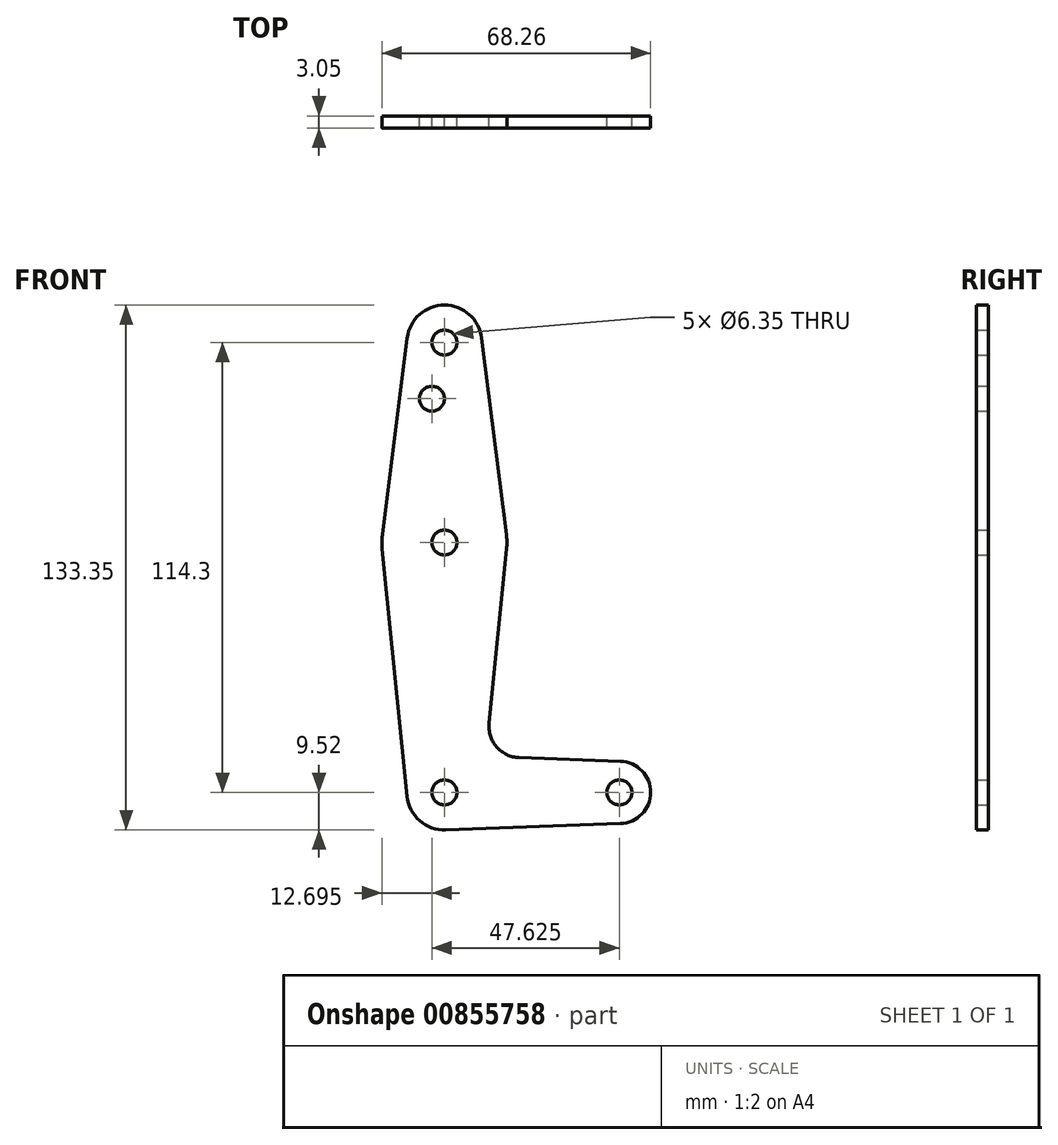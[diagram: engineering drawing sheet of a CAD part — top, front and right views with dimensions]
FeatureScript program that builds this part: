
annotation { "Feature Type Name" : "Feature", "Feature Type Description" : "" }
export const myFeature = defineFeature(function(context is Context, id is Id, definition is map)
    precondition{}
    {
        {
            var Q0;
            Q0=qCreatedBy(makeId("Front.planeOp"),FACE);
            var sketch = newSketch(context, id + "F0", { "sketchPlane" : qUnion([Q0])});
            skCircle(sketch, "E0", {"center": v(0, 0) * mm, "radius": 9.53 * mm});
            skLineSegment(sketch, "E1", {"start": v(0, 0) * mm, "end": v(0, 114.3) * mm, "construction": true});
            skCircle(sketch, "E2", {"center": v(0, 114.3) * mm, "radius": 9.53 * mm});
            skCircle(sketch, "E3", {"center": v(0, 63.5) * mm, "radius": 15.88 * mm});
            skLineSegment(sketch, "E4", {"start": v(0, 0) * mm, "end": v(44.45, 0) * mm, "construction": true});
            skCircle(sketch, "E5", {"center": v(44.45, 0) * mm, "radius": 7.94 * mm});
            skLineSegment(sketch, "E6", {"start": v(-9.45, 115.5) * mm, "end": v(-15.75, 65.48) * mm});
            skLineSegment(sketch, "E7", {"start": v(9.45, 115.5) * mm, "end": v(15.75, 65.48) * mm});
            skLineSegment(sketch, "E8", {"start": v(-15.8, 61.91) * mm, "end": v(-9.48, -0.95) * mm});
            skLineSegment(sketch, "E9", {"start": v(15.8, 61.91) * mm, "end": v(11.34, 17.6) * mm});
            skLineSegment(sketch, "E10", {"start": v(18.97, 8.85) * mm, "end": v(44.73, 7.93) * mm});
            skLineSegment(sketch, "E11", {"start": v(0.34, -9.52) * mm, "end": v(44.73, -7.93) * mm});
            skCircle(sketch, "E12", {"center": v(0, 114.3) * mm, "radius": 3.18 * mm});
            skCircle(sketch, "E13", {"center": v(0, 63.5) * mm, "radius": 3.18 * mm});
            skCircle(sketch, "E14", {"center": v(0, 0) * mm, "radius": 3.18 * mm});
            skCircle(sketch, "E15", {"center": v(44.45, 0) * mm, "radius": 3.18 * mm});
            skCircle(sketch, "E16", {"center": v(-3.18, 100.03) * mm, "radius": 3.18 * mm});
            skArc(sketch, "E17.filletArc", {"start": v(11.34, 17.6) * mm, "mid": v(13.26, 11.57) * mm, "end": v(18.97, 8.85) * mm});
            skSolve(sketch);
        }
        {
            var Q0;
            Q0 = qSketchRegion(id + "F0", true);
            extrude(context, id + "F1", {"entities" : qUnion([Q0]), "depth" : 3.05 * mm, "offsetDistance" : 25.4 * mm});
        }
    });
